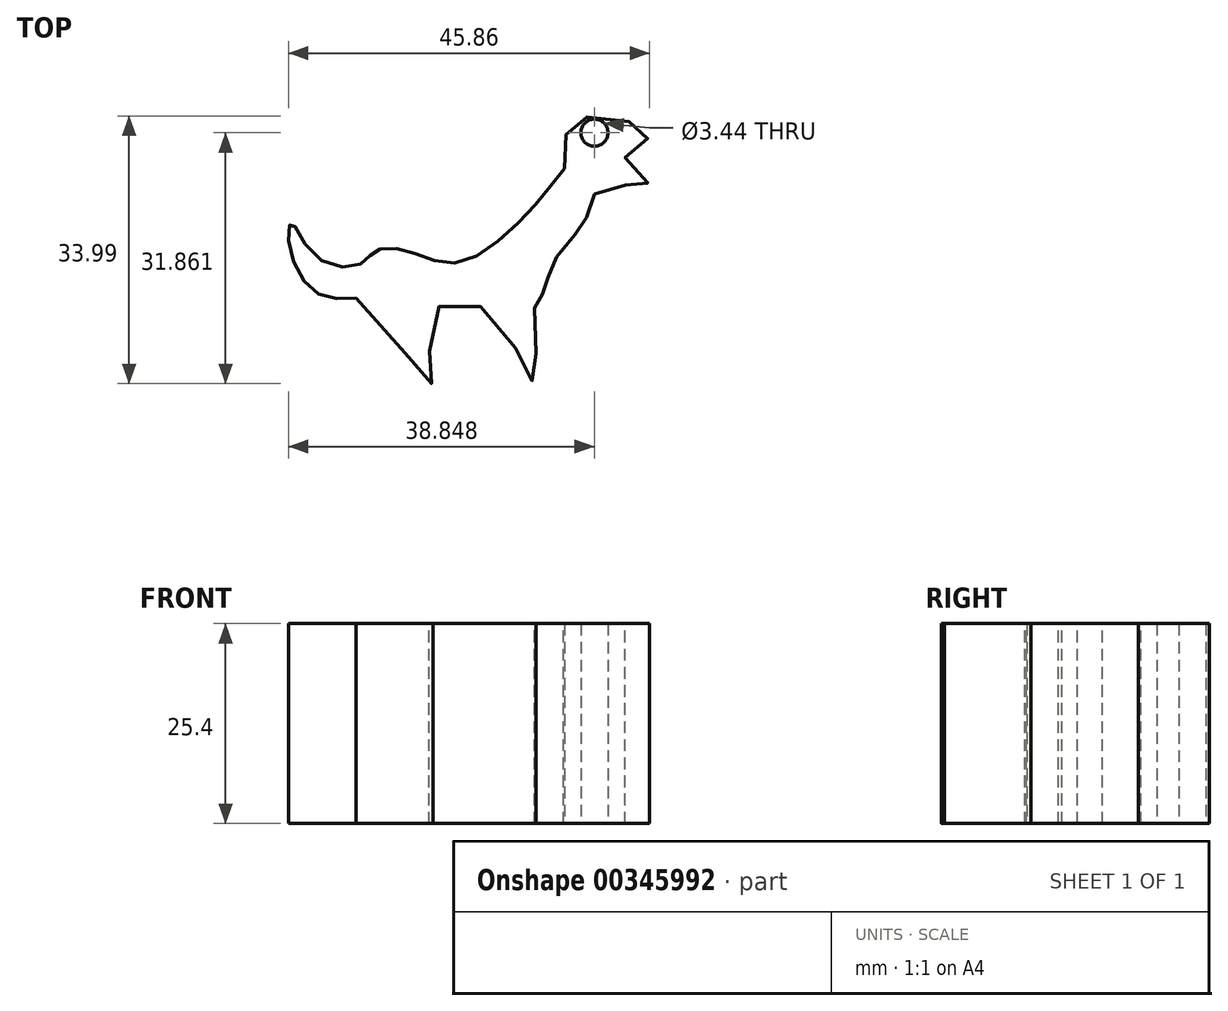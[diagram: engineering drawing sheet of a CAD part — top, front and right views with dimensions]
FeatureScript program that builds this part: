
annotation { "Feature Type Name" : "Feature", "Feature Type Description" : "" }
export const myFeature = defineFeature(function(context is Context, id is Id, definition is map)
    precondition{}
    {
        {
            var Q0;
            Q0=qCreatedBy(makeId("Top.planeOp"),FACE);
            var sketch = newSketch(context, id + "F0", { "sketchPlane" : qUnion([Q0])});
            skFitSpline(sketch, "E0", {"points": [v(-37.25, 42.97) * mm, v(-42.58, 43.85) * mm, v(-45.76, 49.9) * mm, v(-45.45, 52.53) * mm, v(-42.34, 48.23) * mm, v(-36.6, 47.35) * mm, v(-34.86, 48.94) * mm, v(-30.88, 49.02) * mm, v(-24.67, 47.43) * mm, v(-16.47, 52.77) * mm, v(-10.81, 59.45) * mm], "startDerivative": vector(-57.83, -2.57) * mm, "endDerivative": vector(40.12, 51.93) * mm});
            skFitSpline(sketch, "E1", {"points": [v(-10.81, 59.45) * mm, v(-10.18, 64.63) * mm, v(-5.64, 66.06) * mm, v(0, 63.6) * mm, v(-3.1, 60.9) * mm, v(0, 57.27) * mm, v(-5.72, 57.27) * mm, v(-7.47, 54.6) * mm, v(-8.5, 52.37) * mm, v(-9.86, 50.54) * mm, v(-12.5, 47.11) * mm, v(-12.88, 45.2) * mm, v(-13.36, 43.53) * mm, v(-14.16, 43.53) * mm, v(-14.48, 37.72) * mm, v(-14.87, 32.46) * mm, v(-19.97, 40.9) * mm, v(-27.53, 40.9) * mm, v(-27.59, 32.2) * mm, v(-37.25, 42.97) * mm], "startDerivative": vector(-7.6, 108.3) * mm, "endDerivative": vector(-162.66, 142.64) * mm});
            skCircle(sketch, "E2", {"center": v(-7, 64) * mm, "radius": 1.72 * mm});
            skPoint(sketch, "E3.0.internal.orphan", {"position": v(16.66, 52.36) * mm});
            skPoint(sketch, "E4.0.internal.orphan", {"position": v(16.66, 47.11) * mm});
            skPoint(sketch, "E4.10.internal.orphan", {"position": v(23.82, 47.11) * mm});
            skPoint(sketch, "E5.start.orphan", {"position": v(-20.76, 26.1) * mm});
            skPoint(sketch, "E6.start.orphan", {"position": v(-32.48, 26.1) * mm});
            skSolve(sketch);
        }
        {
            var Q0;
            Q0=makeQuery(id+"F0.imprint","IMPRINT",FACE,{"disambiguationData":[TD([[makeQuery(id+"F0.imprint","IMPRINT",EDGE,{"derivedFrom":sQuery(id+"F0.wireOp",EDGE,"E0")}),-1.0]])]});
            extrude(context, id + "F1", {"entities" : qUnion([Q0]), "depth" : 25.4 * mm});
        }
    });
